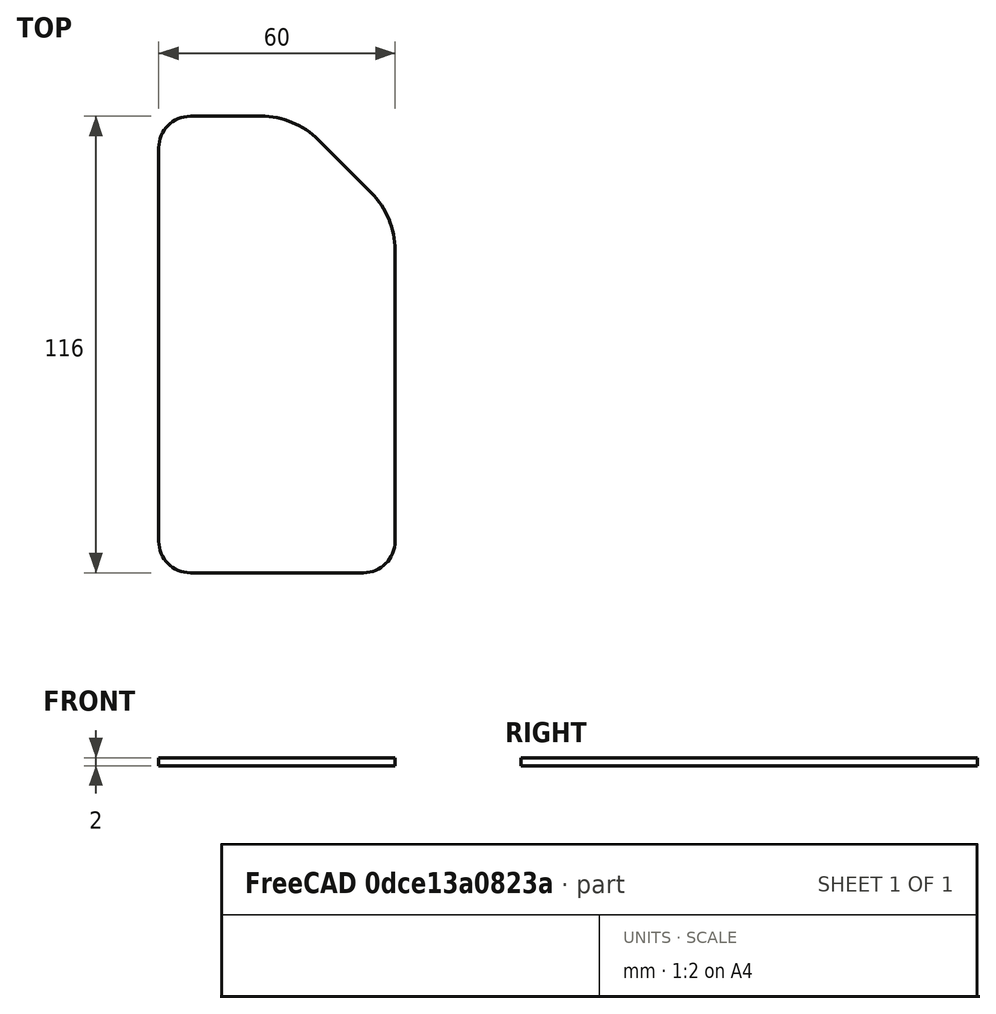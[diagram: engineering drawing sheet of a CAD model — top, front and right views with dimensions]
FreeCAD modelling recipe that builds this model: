
FCSTD DOCUMENT
Label: BackPlate
objects: Sketcher::SketchObject×1, PartDesign::Pad×1
note: 3 computed .brp shape members not serialized (recipe doc carries the construction recipe); baked Part::Feature solids carry a one-line shape summary decoded from their .brp

FEATURE [Sketcher::SketchObject] Sketch
  sketch-geometry (10):
    g0: LineSegment StartX=60 StartY=8 StartZ=0 EndX=60 EndY=82 EndZ=0
    g1: LineSegment StartX=0 StartY=108 StartZ=0 EndX=0 EndY=8 EndZ=0
    g2: LineSegment StartX=8 StartY=116 StartZ=0 EndX=26 EndY=116 EndZ=0
    g3: LineSegment StartX=8 StartY=0 StartZ=0 EndX=52 EndY=0 EndZ=0
    g4: ArcOfCircle CenterX=8 CenterY=108 CenterZ=0 NormalX=0 NormalY=0 NormalZ=1 Radius=8 StartAngle=1.5708 EndAngle=3.14159
    g5: ArcOfCircle CenterX=52 CenterY=8 CenterZ=0 NormalX=0 NormalY=0 NormalZ=1 Radius=8 StartAngle=4.71239 EndAngle=6.28319
    g6: ArcOfCircle CenterX=8 CenterY=8 CenterZ=0 NormalX=0 NormalY=0 NormalZ=1 Radius=8 StartAngle=3.14159 EndAngle=4.71239
    g7: LineSegment StartX=40.5416 StartY=109.977 StartZ=0 EndX=53.9767 EndY=96.5416 EndZ=0
    g8: ArcOfCircle CenterX=26 CenterY=95.435 CenterZ=0 NormalX=0 NormalY=0 NormalZ=1 Radius=20.565 StartAngle=0.7854 EndAngle=1.5708
    g9: ArcOfCircle CenterX=39.435 CenterY=82 CenterZ=0 NormalX=0 NormalY=0 NormalZ=1 Radius=20.565 StartAngle=6.28319 EndAngle=7.06858
  constraints (35):
    c: Vertical(g0)
    c: Vertical(g1)
    c: Horizontal(g2)
    c: Horizontal(g3)
    c: Coincident(g6,g1)
    c: Coincident(g3,g6)
    c: Coincident(g3,g5)
    c: Coincident(g5,g0)
    c: Coincident(g2,g4)
    c: Coincident(g1,g4)
    c: Radius(g4) = 8
    c: Equal(g5,g6)
    c: Tangent(g4,g2)
    c: Tangent(g5,g3)
    c: DistanceX(g1,g0) = 60
    c: DistanceX(g1) = 0
    c: Tangent(g1,g4)
    c: Tangent(g3,g6)
    c: Tangent(g6,g1)
    c: DistanceY(g3) = 0
    c: Angle(g7) = -0.785398
    c: Coincident(g7,g8)
    c: Coincident(g8,g2)
    c: Tangent(g8,g2)
    c: Tangent(g7,g8)
    c: Coincident(g9,g7)
    c: Tangent(g9,g7)
    c: Coincident(g9,g0)
    c: Distance(g7) = 19
    c: Distance(g2) = 18
    c: Equal(g9,g8)
    c: Equal(g4,g6)
    c: Tangent(g0,g9)
    c: Tangent(g5,g0)
    c: DistanceY(g0,g3) = -82
FEATURE [PartDesign::Pad] Pad
  Length = 2
  MirroredExtent = false
  Sketch = -> Sketch
